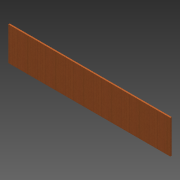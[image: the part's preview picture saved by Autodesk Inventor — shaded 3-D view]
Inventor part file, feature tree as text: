
AUTODESK INVENTOR PART (.ipt)
format: ipt  version: 2013 (Build 170138000, 138)  size: 80,384 bytes
history: native  units: in
note: dims shown in document units (in); Inventor stores cm internally (conversion verified against a paired STEP export)
features: extrude x1, sketch x1
ambient origin geometry x8: Origin, YZ Plane, XZ Plane, XY Plane, X Axis, Y Axis, Z Axis, Center Point
bodies: Solid1 (feature_tree)
feature tree (2):
  extrude  "Extrusion1"  Depth=12.0in
  sketch  "Sketch1"  dims[d0=58.0in d1=12.0in d2=0.5in d3=0.0in]
